# Revit family: QF_BPRO_TWH 1H_575183
name_source: partatom
category: Sonderausstattung
revit_build: Autodesk Revit 2018 (Build: 20181015_0930(x64)
units: mm (PartAtom-declared; Revit-internal decimal feet)

## family parameters
Arbeitsebenenbasiert = Nein
Beim Laden mit Abzugskörper schneiden = Nein
Bemaßung runder Anschluss = Durchmesser verwenden
Gemeinsam genutzt = Nein
Immer vertikal = Ja
Raumberechnungspunkt = Nein
Teiletyp = Normal

## types (1)
- TWH 1H
    Artikel Nummer = 575183
    Beschreibung = TWH 1H
Tellerwagen für 1-seitige Beschickung,
hohe Ausführung,
komplett aus rostfreiem Edelstahl,
inkl. 4 einhängbaren Trennblechen zur
flexiblen Einstellung auf die jeweilige
Tellergröße,
Bordmaß: 858 x 288 mm
Entnahmehöhe unten: 455 mm
Fassungsvermögen: bis zu 150 Teller,
ø 26 cm
    Beschreibung durch Hersteller analog Leistungsverzeichnislangtext = Abmessungen

Länge:			984 mm
Breite:		456 mm  
Höhe:		950 mm


Ausführung

Der Tellerwagen ist komplett aus CNS 18/10 hergestellt. Das Rahmengestell besteht aus stabilem Vierkantrohr 25x25 mm. Dazwischen befindet sich die verschweißte Rückwand und das schräg zur Rückwand geneigte Abstellbord.
Anhand der 4 einhängbaren Trennbleche lassen sich mithilfe des Lochrasters im Boden und der Rückwand die jeweiligen Tellergrößen flexibel einstellen.
Der Wagen ist einseitig beschickbar und passend für Teller mit einem Durchmesser bis max. 260 mm. 

Der Tellerwagen ist fahrbar mittels rostfreien Kunststoffrollen gemäß DIN 18867-8 (4 Lenkrollen, davon 2 mit Feststeller, Rollendurchmesser 125 mm). An allen vier Ecken befinden sich runde Wandabweiser.


Technische Daten

Werkstoff:	CNS 18/10	
Gesamttragfähigkeit:	105 kg	
Kapazität:	150 Teller, passend für 	Teller max. 260 mm <unrecoverable-encoding: 3 bytes ef8386>
	

Besonderheit

•	Inkl. 4 einhängbarenTrennblechen zur flexiblen Einstellung der gewünschten Tellergröße


Fabrikat

Hersteller:			B.PRO
Modell:	TWH 1H
Best.Nr.	575 183
    CE Kennzeichnung = Ja
    Gerätegewicht Netto = 30.00 kg
    Großküchengerätezuordnung = Ja
    Hersteller = B.PRO GmbH
    Höhe = 950 mm
    Internetadresse Gerätehersteller = https://www.bpro-solutions.com
    Kosten = 866.7 $
    Länge Gerätebreite = 984 mm
    Material = QF_Metal-Stainless-Steel_general
    Material Rollen = QF_Plastic-Dark_Grey-Matt
    Material Stoßschutz = QF_Plastic-Dark_Grey-Matt
    Modell = TWH 1H
    Tiefe = 456 mm
    Typenkommentare = Tellerwagen
    URL = https://www.bpro-solutions.com
    Zubehör = Ja
